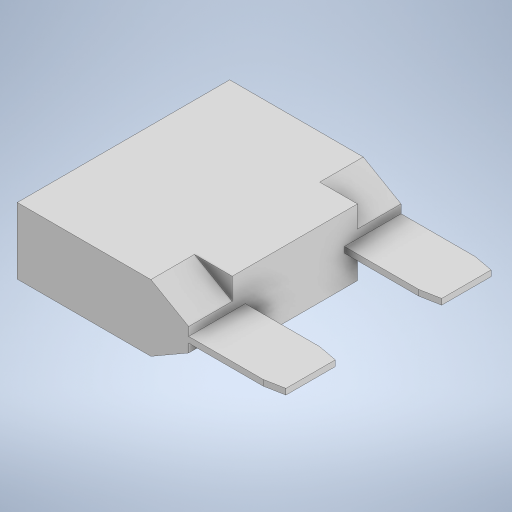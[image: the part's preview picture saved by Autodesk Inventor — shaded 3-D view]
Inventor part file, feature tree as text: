
AUTODESK INVENTOR PART (.ipt)
format: ipt  version: 2023 (Build 270158000, 158)  size: 273,408 bytes
history: native  units: in
note: dims shown in document units (in); Inventor stores cm internally (conversion verified against a paired STEP export)
features: extrude x3, sketch x3, mirror x2
ambient origin geometry x8: Origin, YZ Plane, XZ Plane, XY Plane, X Axis, Y Axis, Z Axis, Center Point
bodies: Solid1 (feature_tree)
feature tree (8):
  extrude  "Extrusion1"  Depth=0.9291in
  extrude  "Extrusion2"  Depth=0.5079in
  extrude  "Extrusion3"  Depth=0.3602in TaperAngle=0.0deg
  mirror  "Mirror1"
  mirror  "Mirror2"
  sketch  "Sketch1"  dims[d0=1.1516in d1=0.9291in]
  sketch  "Sketch2"  dims[d2=0.3071in d3=0.5079in]
  sketch  "Sketch3"  dims[d4=0.0315in d5=0.0in d6=0.3602in d7=0.0157in d8=0.0in d9=0.0in d10=0.2047in d11=0.1181in d12=0.2362in d13=0.0in d14=0.2687in d15=0.5374in d16=0.2677in d17=0.2677in d18=0.1043in d19=0.1043in d20=0.1043in d21=0.1043in d22=0.0197in d23=0.0197in]
